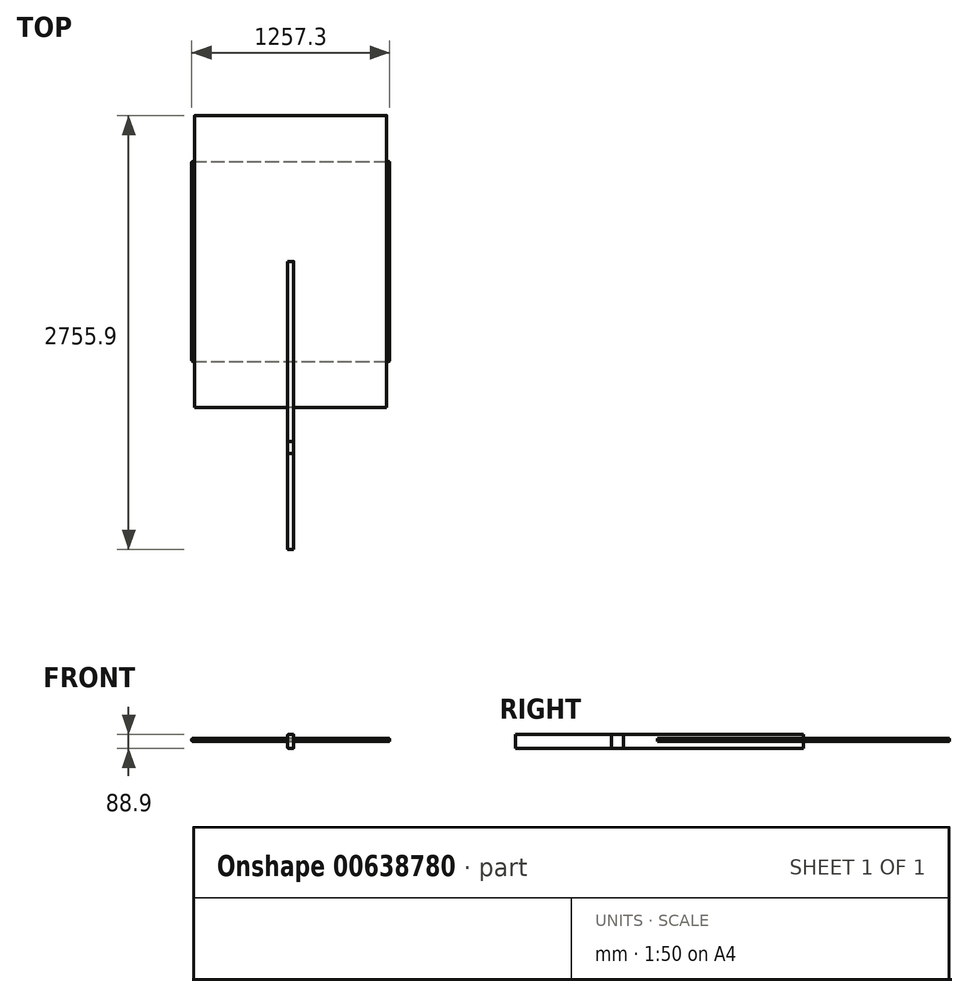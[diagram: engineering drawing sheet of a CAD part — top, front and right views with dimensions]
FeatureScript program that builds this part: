
annotation { "Feature Type Name" : "Feature", "Feature Type Description" : "" }
export const myFeature = defineFeature(function(context is Context, id is Id, definition is map)
    precondition{}
    {
        {
            var Q0;
            Q0=qCreatedBy(makeId("Front.planeOp"),FACE);
            var sketch = newSketch(context, id + "F0", { "sketchPlane" : qUnion([Q0])});
            skLineSegment(sketch, "E0.bottom", {"start": v(15.87, 44.45) * mm, "end": v(-15.88, 44.45) * mm});
            skLineSegment(sketch, "E0.top", {"start": v(15.88, -44.45) * mm, "end": v(-15.87, -44.45) * mm});
            skLineSegment(sketch, "E0.left", {"start": v(19.05, 41.28) * mm, "end": v(19.05, -41.28) * mm});
            skLineSegment(sketch, "E0.right", {"start": v(-19.05, 41.28) * mm, "end": v(-19.05, -41.28) * mm});
            skPoint(sketch, "E0.middle", {"position": v(0, 0) * mm});
            skPoint(sketch, "E1.visualSharp", {"position": v(-19.05, 44.45) * mm});
            skArc(sketch, "E1.filletArc", {"start": v(-15.88, 44.45) * mm, "mid": v(-18.12, 43.52) * mm, "end": v(-19.05, 41.28) * mm});
            skPoint(sketch, "E2.visualSharp", {"position": v(19.05, 44.45) * mm});
            skArc(sketch, "E2.filletArc", {"start": v(19.05, 41.28) * mm, "mid": v(18.12, 43.52) * mm, "end": v(15.87, 44.45) * mm});
            skPoint(sketch, "E3.visualSharp", {"position": v(19.05, -44.45) * mm});
            skArc(sketch, "E3.filletArc", {"start": v(15.88, -44.45) * mm, "mid": v(18.12, -43.52) * mm, "end": v(19.05, -41.28) * mm});
            skPoint(sketch, "E4.visualSharp", {"position": v(-19.05, -44.45) * mm});
            skArc(sketch, "E4.filletArc", {"start": v(-19.05, -41.28) * mm, "mid": v(-18.12, -43.52) * mm, "end": v(-15.87, -44.45) * mm});
            skSolve(sketch);
        }
        {
            var Q0;
            Q0=makeQuery(id+"F0.imprint","IMPRINT",FACE,{"disambiguationData":[TD([[makeQuery(id+"F0.imprint","IMPRINT",EDGE,{"derivedFrom":sQuery(id+"F0.wireOp",EDGE,"E0.bottom")}),1.0]])]});
            extrude(context, id + "F1", {"entities" : qUnion([Q0]), "depth" : 1219.2 * mm, "offsetDistance" : 25.4 * mm});
        }
        {
            var Q0;
            Q0 = qSketchRegion(id + "F0", true);
            extrude(context, id + "F2", {"entities" : qUnion([Q0]), "depth" : 1143 * mm, "offsetDistance" : 25.4 * mm});
        }
        {
            var Q0;
            Q0=qCreatedBy(makeId("Top.planeOp"),FACE);
            var sketch = newSketch(context, id + "F3", { "sketchPlane" : qUnion([Q0])});
            skLineSegment(sketch, "E5.bottom", {"start": v(-628.65, 635) * mm, "end": v(628.65, 635) * mm});
            skLineSegment(sketch, "E5.top", {"start": v(-628.65, -635) * mm, "end": v(628.65, -635) * mm});
            skLineSegment(sketch, "E5.left", {"start": v(-628.65, 635) * mm, "end": v(-628.65, -635) * mm});
            skLineSegment(sketch, "E5.right", {"start": v(628.65, 635) * mm, "end": v(628.65, -635) * mm});
            skPoint(sketch, "E5.middle", {"position": v(0, 0) * mm});
            skSolve(sketch);
        }
        {
            var Q0;
            Q0=makeQuery(id+"F3.imprint","IMPRINT",FACE,{"disambiguationData":[TD([[makeQuery(id+"F3.imprint","IMPRINT",EDGE,{"derivedFrom":sQuery(id+"F3.wireOp",EDGE,"E5.bottom")}),-1.0]])]});
            extrude(context, id + "F4", {"entities" : qUnion([Q0]), "depth" : 19.05 * mm, "offsetDistance" : 25.4 * mm});
        }
        {
            var Q0;
            Q0=makeQuery(id+"F4.opExtrude","CAP_EDGE",EDGE,{"disambiguationData":[OSD([sQuery(id+"F3.wireOp",EDGE,"E5.left")])],"isStart":false});
            var Q1;
            Q1=makeQuery(id+"F4.opExtrude","CAP_EDGE",EDGE,{"disambiguationData":[OSD([sQuery(id+"F3.wireOp",EDGE,"E5.top")])],"isStart":false});
            var Q2;
            Q2=makeQuery(id+"F4.opExtrude","CAP_EDGE",EDGE,{"disambiguationData":[OSD([sQuery(id+"F3.wireOp",EDGE,"E5.bottom")])],"isStart":false});
            var Q3;
            Q3=makeQuery(id+"F4.opExtrude","CAP_EDGE",EDGE,{"disambiguationData":[OSD([sQuery(id+"F3.wireOp",EDGE,"E5.right")])],"isStart":false});
            var Q4;
            Q4=makeQuery(id+"F4.opExtrude","CAP_EDGE",EDGE,{"disambiguationData":[OSD([sQuery(id+"F3.wireOp",EDGE,"E5.right")])],"isStart":true});
            var Q5;
            Q5=makeQuery(id+"F4.opExtrude","CAP_EDGE",EDGE,{"disambiguationData":[OSD([sQuery(id+"F3.wireOp",EDGE,"E5.left")])],"isStart":true});
            fillet(context, id + "F5", {"entities" : qUnion([Q0, Q1, Q2, Q3, Q4, Q5]), "radius" : 6.35 * mm, "tangentPropagation" : true, "allowEdgeOverflow" : false});
        }
        {
            var Q0;
            Q0=makeQuery(id+"F4.opExtrude","CAP_EDGE",EDGE,{"disambiguationData":[OSD([sQuery(id+"F3.wireOp",EDGE,"E5.top")])],"isStart":true});
            var Q1;
            Q1=makeQuery(id+"F4.opExtrude","CAP_EDGE",EDGE,{"disambiguationData":[OSD([sQuery(id+"F3.wireOp",EDGE,"E5.bottom")])],"isStart":true});
            fillet(context, id + "F6", {"entities" : qUnion([Q0, Q1]), "radius" : 6.35 * mm, "tangentPropagation" : true, "allowEdgeOverflow" : false});
        }
        {
            var Q0;
            Q0 = qSketchRegion(id + "F0", true);
            extrude(context, id + "F7", {"entities" : qUnion([Q0]), "depth" : 1828.8 * mm, "offsetDistance" : 25.4 * mm});
        }
        {
            var Q0;
            Q0=qCreatedBy(makeId("Top.planeOp"),FACE);
            var sketch = newSketch(context, id + "F8", { "sketchPlane" : qUnion([Q0])});
            skLineSegment(sketch, "E6.bottom", {"start": v(609.6, 927.1) * mm, "end": v(-609.6, 927.1) * mm});
            skLineSegment(sketch, "E6.top", {"start": v(609.6, -927.1) * mm, "end": v(-609.6, -927.1) * mm});
            skLineSegment(sketch, "E6.left", {"start": v(609.6, 927.1) * mm, "end": v(609.6, -927.1) * mm});
            skLineSegment(sketch, "E6.right", {"start": v(-609.6, 927.1) * mm, "end": v(-609.6, -927.1) * mm});
            skPoint(sketch, "E6.middle", {"position": v(0, 0) * mm});
            skSolve(sketch);
        }
        {
            var Q0;
            Q0 = qSketchRegion(id + "F8", true);
            extrude(context, id + "F9", {"entities" : qUnion([Q0]), "depth" : 19.05 * mm, "offsetDistance" : 25.4 * mm});
        }
        {
            var Q0;
            Q0=makeQuery(id+"F9.opExtrude","CAP_EDGE",EDGE,{"disambiguationData":[OSD([sQuery(id+"F8.wireOp",EDGE,"E6.bottom")])],"isStart":false});
            var Q1;
            Q1=makeQuery(id+"F9.opExtrude","CAP_EDGE",EDGE,{"disambiguationData":[OSD([sQuery(id+"F8.wireOp",EDGE,"E6.bottom")])],"isStart":true});
            fillet(context, id + "F10", {"entities" : qUnion([Q0, Q1]), "radius" : 6.35 * mm, "tangentPropagation" : true, "allowEdgeOverflow" : false});
        }
    });
